# Revit family: KEUCO_17612019004
name_source: partatom
category: Allgemeines Modell
revit_build: Autodesk Revit 2016 (Build: 20150220_1215(x64)
units: mm (PartAtom-declared; Revit-internal decimal feet)

## family parameters
Arbeitsebenenbasiert = Ja
Beim Laden mit Abzugskörper schneiden = Nein
Bemaßung runder Anschluss = Durchmesser verwenden
Gemeinsam genutzt = Nein
Immer vertikal = Nein
Kann Basisbauteil für Bewehrung sein = Nein
Raumberechnungspunkt = Nein
Teiletyp = Normal

## types (2) — shared parameters
Hersteller = KEUCO
Kategorie = ACC
Material Rahmen = Verchromt
Serie = Plan
URL = https://www.keuco.com
Verwendung = GWC / WP
Vorgabe-Ansicht = 1219 mm

## per-type parameters (varying)
| type | Ausschreibungstext | Beschreibung | Gewicht | Material Spiegel | Rechtspiegel | Rundspiegel |
| 17612019004 | KEUCO iLook_move Kosmetikspiegel, 17612019004 
hochwertiger Kosmetikspiegel, rund,
hochglanzverchromt, beleuchtet,
an Schwenkarm aus einem stabilen,
rechteckigen Metallprofil mit verdeckten Hochleistungsscharnieren,
flächige Wandmontage mit 4 Befestigungspunkten
zur optimalen Lastverteilung,
dreidimensional verstellbar, Spiegel einseitig konkav,
Vergrößerungsfaktor x 5,
12V Netzteil und Wipp-Schalter im Wandteil integriert,
Eingangsbereich 220-240 V,
Verkabelung im Schwenkarm integriert,
Beleuchtung: 1 x 4,5 Watt LED (wartungsfrei),
Verbrauch im Standby: 0 Watt,
Bedienung ausschließlich über Raumlichtschalter,
nicht im Lieferumfang enthalten,
1 Lichtfarbe: 6500 Kelvin (Tageslicht),
Höhe der Wandbefestigung ca. 200 mm Breite ca. 45 mm,
maximale Höhe ca. 500 mm,
Außendurchmesser 212 mm, maximale Ausladung ca. 313 mm,
der Kosmetikspiegel wird verdeckt angebracht,
Lieferung inkl. korrosionsfreiem Befestigungsmaterial | beleuchtet, 1 Lichtfarbe 6500 Kelvin (Tageslicht),
Bedienung über Wippschalter,
an dreidimensional verstellbarem Schwenkarm,
Spiegel einseitig, Vergrößerungsfaktor x 5

Bedienung:
mit integriertem Wippschalter

Stromversorgung:
12 V Netzteil im Wandarm integriert,
Eingangsbereich 220 - 240 V

Beleuchtung:
LED 4,5 Watt (Lebensdauer > 50.000 Stunden)
Leuchtmittel nicht austauschbar
EEK: A, 5 kWh/1000h | 1200 | Mirror | Nein | Ja |
| 17613019004 | KEUCO iLook_move Kosmetikspiegel, 17613019004
hochwertiger Kosmetikspiegel, hochglanzverchromt, beleuchtet,
quadratisch, mit elegant gewölbten Kanten, 
an Schwenkarm aus einem stabilen, 
rechteckigen Metallprofil mit verdeckten Hochleistungsscharnieren,
flächige Wandmontage mit 4 Befestigungspunkten 
zur optimalen Lastverteilung,
dreidimensional verstellbar, Spiegel einseitig konkav, 
Vergrößerungsfaktor x 5,
12V Netzteil und Wipp-Schalter im Wandteil integriert 
Eingangsbereich 220-240V,
Verkabelung im Schwenkarm integriert,
Beleuchtung: 7 Watt LED (wartungsfrei), 
Verbrauch im Standby: 0 Watt,
1 Lichtfarbe: 6500 Kelvin (Tageslicht),
Höhe der Wandbefestigung  ca. 200 mm, Breite ca. 45 mm,
maximale Höhe ca. 500 mm,
Außenmaße: 200 x 200 mm, maximale Ausladung ca. 300 mm,
der Kosmetikspiegel wird verdeckt angebracht,
Lieferung inkl. korrosionsfreiem Befestigungsmaterial | beleuchtet, 1 Lichtfarbe 6500 Kelvin (Tageslicht),
Bedienung über Wippschalter,
an dreidimensional verstellbarem Schwenkarm,
Spiegel einseitig, Vergrößerungsfaktor x 5

Bedienung:
mit integriertem Wippschalter

Stromversorgung:
12 V Netzteil im Wandarm integriert,
Eingangsbereich 220 - 240 V

Beleuchtung:
LED 7 Watt (Lebensdauer > 50.000 Stunden)
Leuchtmittel nicht austauschbar
EEK: A, 8 kWh/1000h | 1300 | Spiegel | Ja | Nein |

note: column(s) folded — value = type name in every type: Artikelnummer

## geometry (parser evidence)
native form markers: Sweep x3
no freeform markers — native parametric forms only
